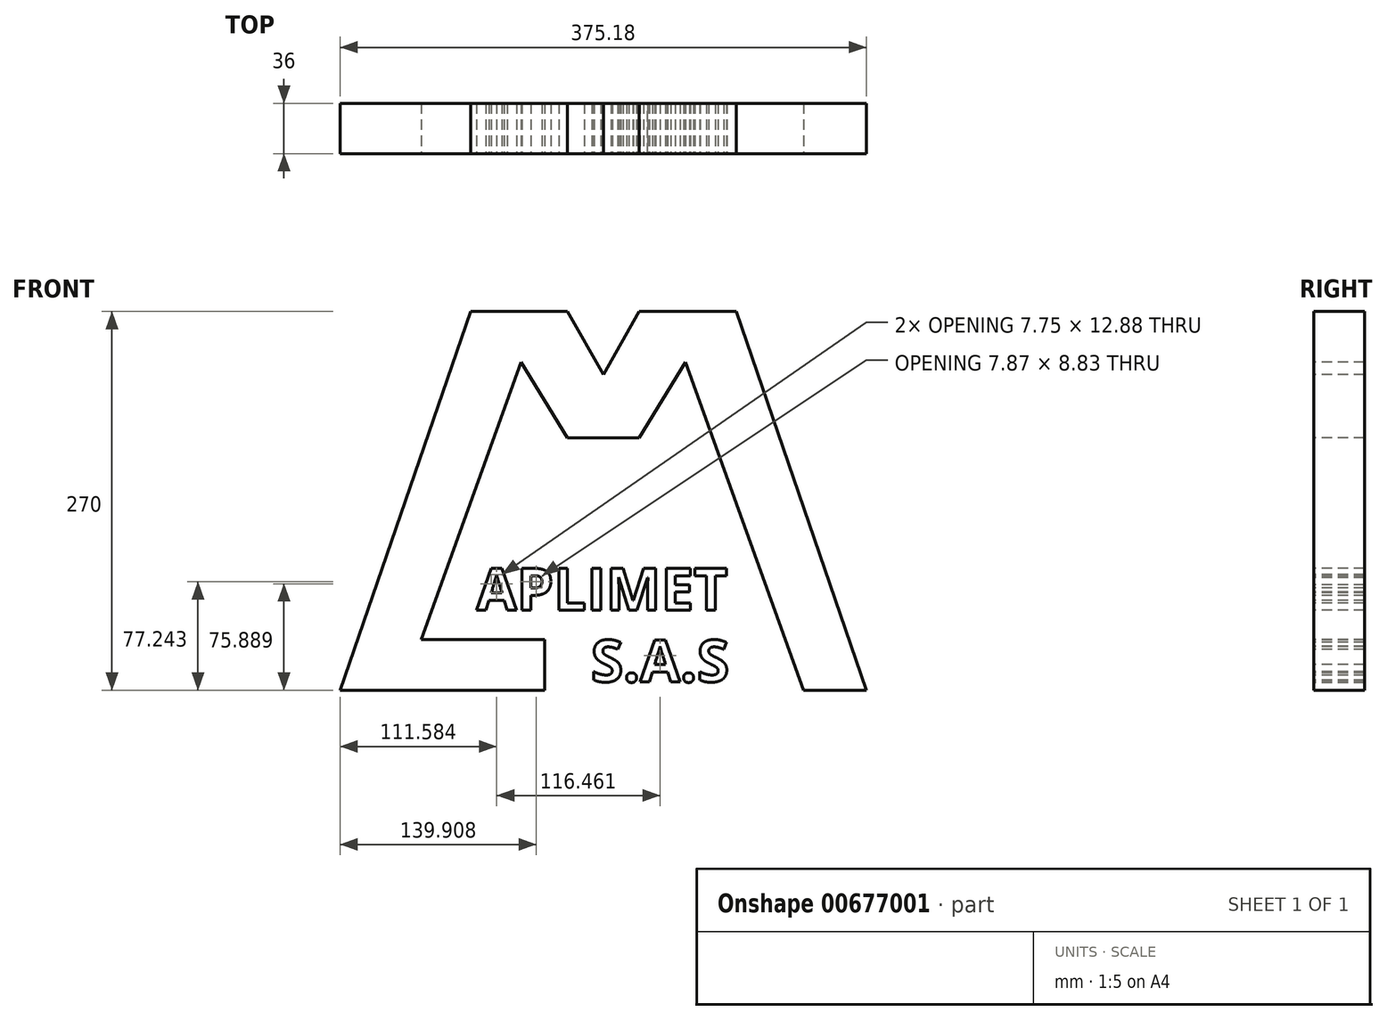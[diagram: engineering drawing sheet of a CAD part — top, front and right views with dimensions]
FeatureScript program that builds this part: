
annotation { "Feature Type Name" : "Feature", "Feature Type Description" : "" }
export const myFeature = defineFeature(function(context is Context, id is Id, definition is map)
    precondition{}
    {
        {
            var Q0;
            Q0=qCreatedBy(makeId("Front.planeOp"),FACE);
            var sketch = newSketch(context, id + "F0", { "sketchPlane" : qUnion([Q0])});
            skLineSegment(sketch, "E0", {"start": v(-62.53, -33.33) * mm, "end": v(-31.54, 56.67) * mm});
            skLineSegment(sketch, "E1", {"start": v(-31.54, 56.67) * mm, "end": v(-8.54, 56.67) * mm});
            skLineSegment(sketch, "E2", {"start": v(-8.54, 56.67) * mm, "end": v(0, 41.67) * mm});
            skLineSegment(sketch, "E3", {"start": v(0, 41.67) * mm, "end": v(8.54, 56.67) * mm});
            skLineSegment(sketch, "E4", {"start": v(8.54, 56.67) * mm, "end": v(31.54, 56.67) * mm});
            skLineSegment(sketch, "E5", {"start": v(31.54, 56.67) * mm, "end": v(62.53, -33.33) * mm});
            skLineSegment(sketch, "E6", {"start": v(62.53, -33.33) * mm, "end": v(47.53, -33.33) * mm});
            skLineSegment(sketch, "E7", {"start": v(-62.53, -33.33) * mm, "end": v(-13.89, -33.33) * mm});
            skLineSegment(sketch, "E8", {"start": v(0, 41.67) * mm, "end": v(0, 56.67) * mm, "construction": true});
            skPoint(sketch, "E9.startSnap0", {"position": v(-20.04, 56.67) * mm});
            skLineSegment(sketch, "E10", {"start": v(0, 26.67) * mm, "end": v(8.54, 26.67) * mm});
            skLineSegment(sketch, "E11", {"start": v(0, 26.67) * mm, "end": v(-8.54, 26.67) * mm});
            skLineSegment(sketch, "E12", {"start": v(-19.54, 44.67) * mm, "end": v(-43.22, -21.33) * mm});
            skLineSegment(sketch, "E13", {"start": v(-19.54, 44.67) * mm, "end": v(-8.54, 26.67) * mm});
            skLineSegment(sketch, "E14", {"start": v(8.54, 26.67) * mm, "end": v(19.54, 44.67) * mm});
            skPoint(sketch, "E14.endSnap0", {"position": v(20.04, 56.67) * mm});
            skLineSegment(sketch, "E15", {"start": v(19.54, 44.67) * mm, "end": v(47.53, -33.33) * mm});
            skLineSegment(sketch, "E16", {"start": v(-43.22, -21.33) * mm, "end": v(-13.89, -21.33) * mm});
            skPoint(sketch, "E17.orphan", {"position": v(-47.53, -33.33) * mm});
            skLineSegment(sketch, "E18", {"start": v(-13.89, -21.33) * mm, "end": v(-13.89, -33.33) * mm});
            skSolve(sketch);
        }
        {
            var Q0;
            Q0=makeQuery(id+"F0.imprint","IMPRINT",FACE,{"disambiguationData":[TD([[makeQuery(id+"F0.imprint","IMPRINT",EDGE,{"derivedFrom":sQuery(id+"F0.wireOp",EDGE,"E0")}),-1.0]])]});
            extrude(context, id + "F1", {"entities" : qUnion([Q0]), "oppositeDirection" : true, "depth" : 12 * mm, "offsetDistance" : 25 * mm});
        }
        {
            var Q0;
            Q0=makeQuery(id+"F1.opExtrude","CAP_FACE",FACE,{"disambiguationData":[OSD([sQuery(id+"F0.wireOp",EDGE,"E0"),sQuery(id+"F0.wireOp",EDGE,"E1"),sQuery(id+"F0.wireOp",EDGE,"E2"),sQuery(id+"F0.wireOp",EDGE,"E3"),sQuery(id+"F0.wireOp",EDGE,"E4"),sQuery(id+"F0.wireOp",EDGE,"E5"),sQuery(id+"F0.wireOp",EDGE,"E6"),sQuery(id+"F0.wireOp",EDGE,"E7"),sQuery(id+"F0.wireOp",EDGE,"E10"),sQuery(id+"F0.wireOp",EDGE,"E11"),sQuery(id+"F0.wireOp",EDGE,"E12"),sQuery(id+"F0.wireOp",EDGE,"E13"),sQuery(id+"F0.wireOp",EDGE,"E14"),sQuery(id+"F0.wireOp",EDGE,"E15"),sQuery(id+"F0.wireOp",EDGE,"E16"),sQuery(id+"F0.wireOp",EDGE,"E18")])],"isStart":true});
            var sketch = newSketch(context, id + "F2", { "sketchPlane" : qUnion([Q0])});
            skText(sketch, "E19", { "text": "APLIMET", "fontName": "OpenSans-Bold.ttf"});
            skText(sketch, "E20", { "text": "S.A.S", "fontName": "OpenSans-Bold.ttf"});
            const initialGuessF2  = {"E19": [-0.03014, -0.0143, 1, 0, 0.01], "E20": [-0.00293, -0.03133, 1, 0, 0.01]};
            skSetInitialGuess(sketch, initialGuessF2);
            skSolve(sketch);
        }
        {
            var Q0;
            Q0 = qSketchRegion(id + "F2", true);
            extrude(context, id + "F3", {"entities" : qUnion([Q0]), "oppositeDirection" : true, "depth" : 12 * mm, "offsetDistance" : 25 * mm});
        }
        {
            var Q0;
            Q0=makeQuery(id+"F1.opExtrude","CAP_FACE",FACE,{"disambiguationData":[OSD([sQuery(id+"F0.wireOp",EDGE,"E0"),sQuery(id+"F0.wireOp",EDGE,"E1"),sQuery(id+"F0.wireOp",EDGE,"E2"),sQuery(id+"F0.wireOp",EDGE,"E3"),sQuery(id+"F0.wireOp",EDGE,"E4"),sQuery(id+"F0.wireOp",EDGE,"E5"),sQuery(id+"F0.wireOp",EDGE,"E6"),sQuery(id+"F0.wireOp",EDGE,"E7"),sQuery(id+"F0.wireOp",EDGE,"E10"),sQuery(id+"F0.wireOp",EDGE,"E11"),sQuery(id+"F0.wireOp",EDGE,"E12"),sQuery(id+"F0.wireOp",EDGE,"E13"),sQuery(id+"F0.wireOp",EDGE,"E14"),sQuery(id+"F0.wireOp",EDGE,"E15"),sQuery(id+"F0.wireOp",EDGE,"E16"),sQuery(id+"F0.wireOp",EDGE,"E18")])],"isStart":true});
            var Q1;
            Q1=makeQuery(id+"F1.opExtrude","CAP_FACE",FACE,{"disambiguationData":[OSD([sQuery(id+"F0.wireOp",EDGE,"E0"),sQuery(id+"F0.wireOp",EDGE,"E1"),sQuery(id+"F0.wireOp",EDGE,"E2"),sQuery(id+"F0.wireOp",EDGE,"E3"),sQuery(id+"F0.wireOp",EDGE,"E4"),sQuery(id+"F0.wireOp",EDGE,"E5"),sQuery(id+"F0.wireOp",EDGE,"E6"),sQuery(id+"F0.wireOp",EDGE,"E7"),sQuery(id+"F0.wireOp",EDGE,"E10"),sQuery(id+"F0.wireOp",EDGE,"E11"),sQuery(id+"F0.wireOp",EDGE,"E12"),sQuery(id+"F0.wireOp",EDGE,"E13"),sQuery(id+"F0.wireOp",EDGE,"E14"),sQuery(id+"F0.wireOp",EDGE,"E15"),sQuery(id+"F0.wireOp",EDGE,"E16"),sQuery(id+"F0.wireOp",EDGE,"E18")])],"isStart":false});
            cPlane(context, id + "F4", {"entities" : qUnion([Q0, Q1]), "cplaneType" : CPlaneType.MID_PLANE, "offset" : 25 * mm, "width" : 150 * mm, "height" : 150 * mm});
        }
        {
            var Q0;
            Q0=makeQuery(id+"F1.opExtrude","SWEPT_BODY",BODY,{"disambiguationData":[OSD([sQuery(id+"F0.wireOp",EDGE,"E0"),sQuery(id+"F0.wireOp",EDGE,"E1"),sQuery(id+"F0.wireOp",EDGE,"E2"),sQuery(id+"F0.wireOp",EDGE,"E3"),sQuery(id+"F0.wireOp",EDGE,"E4"),sQuery(id+"F0.wireOp",EDGE,"E5"),sQuery(id+"F0.wireOp",EDGE,"E6"),sQuery(id+"F0.wireOp",EDGE,"E7"),sQuery(id+"F0.wireOp",EDGE,"E10"),sQuery(id+"F0.wireOp",EDGE,"E11"),sQuery(id+"F0.wireOp",EDGE,"E12"),sQuery(id+"F0.wireOp",EDGE,"E13"),sQuery(id+"F0.wireOp",EDGE,"E14"),sQuery(id+"F0.wireOp",EDGE,"E15"),sQuery(id+"F0.wireOp",EDGE,"E16"),sQuery(id+"F0.wireOp",EDGE,"E18")])]});
            var Q1;
            Q1=makeQuery(id+"F3.opExtrude","SWEPT_BODY",BODY,{"disambiguationData":[OSD([sQuery(id+"F2.wireOp",EDGE,"E19.sketch_text.stroke-0"),sQuery(id+"F2.wireOp",EDGE,"E19.sketch_text.stroke-1"),sQuery(id+"F2.wireOp",EDGE,"E19.sketch_text.stroke-2"),sQuery(id+"F2.wireOp",EDGE,"E19.sketch_text.stroke-3"),sQuery(id+"F2.wireOp",EDGE,"E19.sketch_text.stroke-4"),sQuery(id+"F2.wireOp",EDGE,"E19.sketch_text.stroke-5"),sQuery(id+"F2.wireOp",EDGE,"E19.sketch_text.stroke-6"),sQuery(id+"F2.wireOp",EDGE,"E19.sketch_text.stroke-7"),sQuery(id+"F2.wireOp",EDGE,"E19.sketch_text.stroke-8"),sQuery(id+"F2.wireOp",EDGE,"E19.sketch_text.stroke-9"),sQuery(id+"F2.wireOp",EDGE,"E19.sketch_text.stroke-10"),sQuery(id+"F2.wireOp",EDGE,"E19.sketch_text.stroke-11")])]});
            var Q2;
            Q2=makeQuery(id+"F3.opExtrude","SWEPT_BODY",BODY,{"disambiguationData":[OSD([sQuery(id+"F2.wireOp",EDGE,"E19.sketch_text.stroke-12"),sQuery(id+"F2.wireOp",EDGE,"E19.sketch_text.stroke-13"),sQuery(id+"F2.wireOp",EDGE,"E19.sketch_text.stroke-14"),sQuery(id+"F2.wireOp",EDGE,"E19.sketch_text.stroke-15"),sQuery(id+"F2.wireOp",EDGE,"E19.sketch_text.stroke-16"),sQuery(id+"F2.wireOp",EDGE,"E19.sketch_text.stroke-17"),sQuery(id+"F2.wireOp",EDGE,"E19.sketch_text.stroke-18"),sQuery(id+"F2.wireOp",EDGE,"E19.sketch_text.stroke-19"),sQuery(id+"F2.wireOp",EDGE,"E19.sketch_text.stroke-20"),sQuery(id+"F2.wireOp",EDGE,"E19.sketch_text.stroke-21"),sQuery(id+"F2.wireOp",EDGE,"E19.sketch_text.stroke-22"),sQuery(id+"F2.wireOp",EDGE,"E19.sketch_text.stroke-23"),sQuery(id+"F2.wireOp",EDGE,"E19.sketch_text.stroke-24"),sQuery(id+"F2.wireOp",EDGE,"E19.sketch_text.stroke-25"),sQuery(id+"F2.wireOp",EDGE,"E19.sketch_text.stroke-26"),sQuery(id+"F2.wireOp",EDGE,"E19.sketch_text.stroke-27")])]});
            var Q3;
            Q3=makeQuery(id+"F3.opExtrude","SWEPT_BODY",BODY,{"disambiguationData":[OSD([sQuery(id+"F2.wireOp",EDGE,"E19.sketch_text.stroke-28"),sQuery(id+"F2.wireOp",EDGE,"E19.sketch_text.stroke-29"),sQuery(id+"F2.wireOp",EDGE,"E19.sketch_text.stroke-30"),sQuery(id+"F2.wireOp",EDGE,"E19.sketch_text.stroke-31"),sQuery(id+"F2.wireOp",EDGE,"E19.sketch_text.stroke-32"),sQuery(id+"F2.wireOp",EDGE,"E19.sketch_text.stroke-33")])]});
            var Q4;
            Q4=makeQuery(id+"F3.opExtrude","SWEPT_BODY",BODY,{"disambiguationData":[OSD([sQuery(id+"F2.wireOp",EDGE,"E19.sketch_text.stroke-34"),sQuery(id+"F2.wireOp",EDGE,"E19.sketch_text.stroke-35"),sQuery(id+"F2.wireOp",EDGE,"E19.sketch_text.stroke-36"),sQuery(id+"F2.wireOp",EDGE,"E19.sketch_text.stroke-37")])]});
            var Q5;
            Q5=makeQuery(id+"F3.opExtrude","SWEPT_BODY",BODY,{"disambiguationData":[OSD([sQuery(id+"F2.wireOp",EDGE,"E19.sketch_text.stroke-38"),sQuery(id+"F2.wireOp",EDGE,"E19.sketch_text.stroke-39"),sQuery(id+"F2.wireOp",EDGE,"E19.sketch_text.stroke-40"),sQuery(id+"F2.wireOp",EDGE,"E19.sketch_text.stroke-41"),sQuery(id+"F2.wireOp",EDGE,"E19.sketch_text.stroke-42"),sQuery(id+"F2.wireOp",EDGE,"E19.sketch_text.stroke-43"),sQuery(id+"F2.wireOp",EDGE,"E19.sketch_text.stroke-44"),sQuery(id+"F2.wireOp",EDGE,"E19.sketch_text.stroke-45"),sQuery(id+"F2.wireOp",EDGE,"E19.sketch_text.stroke-46"),sQuery(id+"F2.wireOp",EDGE,"E19.sketch_text.stroke-47"),sQuery(id+"F2.wireOp",EDGE,"E19.sketch_text.stroke-48"),sQuery(id+"F2.wireOp",EDGE,"E19.sketch_text.stroke-49"),sQuery(id+"F2.wireOp",EDGE,"E19.sketch_text.stroke-50"),sQuery(id+"F2.wireOp",EDGE,"E19.sketch_text.stroke-51"),sQuery(id+"F2.wireOp",EDGE,"E19.sketch_text.stroke-52"),sQuery(id+"F2.wireOp",EDGE,"E19.sketch_text.stroke-53"),sQuery(id+"F2.wireOp",EDGE,"E19.sketch_text.stroke-54"),sQuery(id+"F2.wireOp",EDGE,"E19.sketch_text.stroke-55"),sQuery(id+"F2.wireOp",EDGE,"E19.sketch_text.stroke-56")])]});
            var Q6;
            Q6=makeQuery(id+"F3.opExtrude","SWEPT_BODY",BODY,{"disambiguationData":[OSD([sQuery(id+"F2.wireOp",EDGE,"E19.sketch_text.stroke-57"),sQuery(id+"F2.wireOp",EDGE,"E19.sketch_text.stroke-58"),sQuery(id+"F2.wireOp",EDGE,"E19.sketch_text.stroke-59"),sQuery(id+"F2.wireOp",EDGE,"E19.sketch_text.stroke-60"),sQuery(id+"F2.wireOp",EDGE,"E19.sketch_text.stroke-61"),sQuery(id+"F2.wireOp",EDGE,"E19.sketch_text.stroke-62"),sQuery(id+"F2.wireOp",EDGE,"E19.sketch_text.stroke-63"),sQuery(id+"F2.wireOp",EDGE,"E19.sketch_text.stroke-64"),sQuery(id+"F2.wireOp",EDGE,"E19.sketch_text.stroke-65"),sQuery(id+"F2.wireOp",EDGE,"E19.sketch_text.stroke-66"),sQuery(id+"F2.wireOp",EDGE,"E19.sketch_text.stroke-67"),sQuery(id+"F2.wireOp",EDGE,"E19.sketch_text.stroke-68")])]});
            var Q7;
            Q7=makeQuery(id+"F3.opExtrude","SWEPT_BODY",BODY,{"disambiguationData":[OSD([sQuery(id+"F2.wireOp",EDGE,"E19.sketch_text.stroke-69"),sQuery(id+"F2.wireOp",EDGE,"E19.sketch_text.stroke-70"),sQuery(id+"F2.wireOp",EDGE,"E19.sketch_text.stroke-71"),sQuery(id+"F2.wireOp",EDGE,"E19.sketch_text.stroke-72"),sQuery(id+"F2.wireOp",EDGE,"E19.sketch_text.stroke-73"),sQuery(id+"F2.wireOp",EDGE,"E19.sketch_text.stroke-74"),sQuery(id+"F2.wireOp",EDGE,"E19.sketch_text.stroke-75"),sQuery(id+"F2.wireOp",EDGE,"E19.sketch_text.stroke-76")])]});
            var Q8;
            Q8=makeQuery(id+"F3.opExtrude","SWEPT_BODY",BODY,{"disambiguationData":[OSD([sQuery(id+"F2.wireOp",EDGE,"E20.sketch_text.stroke-0"),sQuery(id+"F2.wireOp",EDGE,"E20.sketch_text.stroke-1"),sQuery(id+"F2.wireOp",EDGE,"E20.sketch_text.stroke-2"),sQuery(id+"F2.wireOp",EDGE,"E20.sketch_text.stroke-3"),sQuery(id+"F2.wireOp",EDGE,"E20.sketch_text.stroke-4"),sQuery(id+"F2.wireOp",EDGE,"E20.sketch_text.stroke-5"),sQuery(id+"F2.wireOp",EDGE,"E20.sketch_text.stroke-6"),sQuery(id+"F2.wireOp",EDGE,"E20.sketch_text.stroke-7"),sQuery(id+"F2.wireOp",EDGE,"E20.sketch_text.stroke-8"),sQuery(id+"F2.wireOp",EDGE,"E20.sketch_text.stroke-9"),sQuery(id+"F2.wireOp",EDGE,"E20.sketch_text.stroke-10"),sQuery(id+"F2.wireOp",EDGE,"E20.sketch_text.stroke-11"),sQuery(id+"F2.wireOp",EDGE,"E20.sketch_text.stroke-12"),sQuery(id+"F2.wireOp",EDGE,"E20.sketch_text.stroke-13"),sQuery(id+"F2.wireOp",EDGE,"E20.sketch_text.stroke-14"),sQuery(id+"F2.wireOp",EDGE,"E20.sketch_text.stroke-15"),sQuery(id+"F2.wireOp",EDGE,"E20.sketch_text.stroke-16"),sQuery(id+"F2.wireOp",EDGE,"E20.sketch_text.stroke-17"),sQuery(id+"F2.wireOp",EDGE,"E20.sketch_text.stroke-18"),sQuery(id+"F2.wireOp",EDGE,"E20.sketch_text.stroke-19"),sQuery(id+"F2.wireOp",EDGE,"E20.sketch_text.stroke-20"),sQuery(id+"F2.wireOp",EDGE,"E20.sketch_text.stroke-21"),sQuery(id+"F2.wireOp",EDGE,"E20.sketch_text.stroke-22"),sQuery(id+"F2.wireOp",EDGE,"E20.sketch_text.stroke-23"),sQuery(id+"F2.wireOp",EDGE,"E20.sketch_text.stroke-24"),sQuery(id+"F2.wireOp",EDGE,"E20.sketch_text.stroke-25"),sQuery(id+"F2.wireOp",EDGE,"E20.sketch_text.stroke-26"),sQuery(id+"F2.wireOp",EDGE,"E20.sketch_text.stroke-27")])]});
            var Q9;
            Q9=makeQuery(id+"F3.opExtrude","SWEPT_BODY",BODY,{"disambiguationData":[OSD([sQuery(id+"F2.wireOp",EDGE,"E20.sketch_text.stroke-28"),sQuery(id+"F2.wireOp",EDGE,"E20.sketch_text.stroke-29"),sQuery(id+"F2.wireOp",EDGE,"E20.sketch_text.stroke-30"),sQuery(id+"F2.wireOp",EDGE,"E20.sketch_text.stroke-31"),sQuery(id+"F2.wireOp",EDGE,"E20.sketch_text.stroke-32"),sQuery(id+"F2.wireOp",EDGE,"E20.sketch_text.stroke-33"),sQuery(id+"F2.wireOp",EDGE,"E20.sketch_text.stroke-34"),sQuery(id+"F2.wireOp",EDGE,"E20.sketch_text.stroke-35")])]});
            var Q10;
            Q10=makeQuery(id+"F3.opExtrude","SWEPT_BODY",BODY,{"disambiguationData":[OSD([sQuery(id+"F2.wireOp",EDGE,"E20.sketch_text.stroke-36"),sQuery(id+"F2.wireOp",EDGE,"E20.sketch_text.stroke-37"),sQuery(id+"F2.wireOp",EDGE,"E20.sketch_text.stroke-38"),sQuery(id+"F2.wireOp",EDGE,"E20.sketch_text.stroke-39"),sQuery(id+"F2.wireOp",EDGE,"E20.sketch_text.stroke-40"),sQuery(id+"F2.wireOp",EDGE,"E20.sketch_text.stroke-41"),sQuery(id+"F2.wireOp",EDGE,"E20.sketch_text.stroke-42"),sQuery(id+"F2.wireOp",EDGE,"E20.sketch_text.stroke-43"),sQuery(id+"F2.wireOp",EDGE,"E20.sketch_text.stroke-44"),sQuery(id+"F2.wireOp",EDGE,"E20.sketch_text.stroke-45"),sQuery(id+"F2.wireOp",EDGE,"E20.sketch_text.stroke-46"),sQuery(id+"F2.wireOp",EDGE,"E20.sketch_text.stroke-47")])]});
            var Q11;
            Q11=makeQuery(id+"F3.opExtrude","SWEPT_BODY",BODY,{"disambiguationData":[OSD([sQuery(id+"F2.wireOp",EDGE,"E20.sketch_text.stroke-48"),sQuery(id+"F2.wireOp",EDGE,"E20.sketch_text.stroke-49"),sQuery(id+"F2.wireOp",EDGE,"E20.sketch_text.stroke-50"),sQuery(id+"F2.wireOp",EDGE,"E20.sketch_text.stroke-51"),sQuery(id+"F2.wireOp",EDGE,"E20.sketch_text.stroke-52"),sQuery(id+"F2.wireOp",EDGE,"E20.sketch_text.stroke-53"),sQuery(id+"F2.wireOp",EDGE,"E20.sketch_text.stroke-54"),sQuery(id+"F2.wireOp",EDGE,"E20.sketch_text.stroke-55")])]});
            var Q12;
            Q12=makeQuery(id+"F3.opExtrude","SWEPT_BODY",BODY,{"disambiguationData":[OSD([sQuery(id+"F2.wireOp",EDGE,"E20.sketch_text.stroke-56"),sQuery(id+"F2.wireOp",EDGE,"E20.sketch_text.stroke-57"),sQuery(id+"F2.wireOp",EDGE,"E20.sketch_text.stroke-58"),sQuery(id+"F2.wireOp",EDGE,"E20.sketch_text.stroke-59"),sQuery(id+"F2.wireOp",EDGE,"E20.sketch_text.stroke-60"),sQuery(id+"F2.wireOp",EDGE,"E20.sketch_text.stroke-61"),sQuery(id+"F2.wireOp",EDGE,"E20.sketch_text.stroke-62"),sQuery(id+"F2.wireOp",EDGE,"E20.sketch_text.stroke-63"),sQuery(id+"F2.wireOp",EDGE,"E20.sketch_text.stroke-64"),sQuery(id+"F2.wireOp",EDGE,"E20.sketch_text.stroke-65"),sQuery(id+"F2.wireOp",EDGE,"E20.sketch_text.stroke-66"),sQuery(id+"F2.wireOp",EDGE,"E20.sketch_text.stroke-67"),sQuery(id+"F2.wireOp",EDGE,"E20.sketch_text.stroke-68"),sQuery(id+"F2.wireOp",EDGE,"E20.sketch_text.stroke-69"),sQuery(id+"F2.wireOp",EDGE,"E20.sketch_text.stroke-70"),sQuery(id+"F2.wireOp",EDGE,"E20.sketch_text.stroke-71"),sQuery(id+"F2.wireOp",EDGE,"E20.sketch_text.stroke-72"),sQuery(id+"F2.wireOp",EDGE,"E20.sketch_text.stroke-73"),sQuery(id+"F2.wireOp",EDGE,"E20.sketch_text.stroke-74"),sQuery(id+"F2.wireOp",EDGE,"E20.sketch_text.stroke-75"),sQuery(id+"F2.wireOp",EDGE,"E20.sketch_text.stroke-76"),sQuery(id+"F2.wireOp",EDGE,"E20.sketch_text.stroke-77"),sQuery(id+"F2.wireOp",EDGE,"E20.sketch_text.stroke-78"),sQuery(id+"F2.wireOp",EDGE,"E20.sketch_text.stroke-79"),sQuery(id+"F2.wireOp",EDGE,"E20.sketch_text.stroke-80"),sQuery(id+"F2.wireOp",EDGE,"E20.sketch_text.stroke-81"),sQuery(id+"F2.wireOp",EDGE,"E20.sketch_text.stroke-82"),sQuery(id+"F2.wireOp",EDGE,"E20.sketch_text.stroke-83")])]});
            var Q13;
            Q13=qCreatedBy(makeId("Origin.pointOp"),VERTEX);
            transform(context, id + "F5", {"entities" : qUnion([Q0, Q1, Q2, Q3, Q4, Q5, Q6, Q7, Q8, Q9, Q10, Q11, Q12]), "transformType" : TransformType.SCALE_UNIFORMLY, "scale" : 3, "scalePoint" : qUnion([Q13]), "makeCopy" : false});
        }
    });
